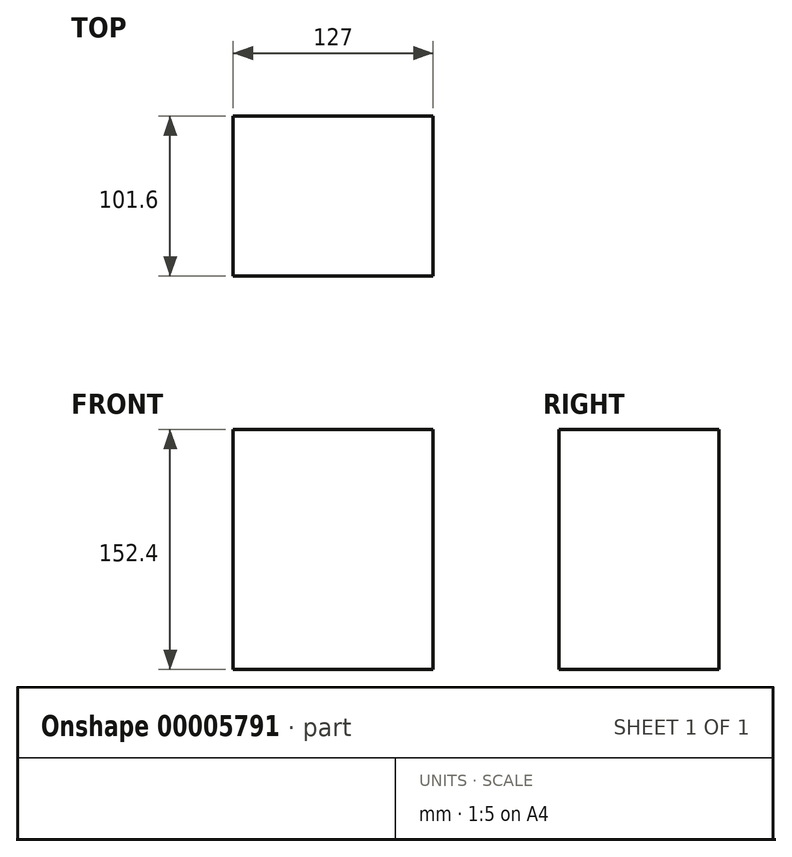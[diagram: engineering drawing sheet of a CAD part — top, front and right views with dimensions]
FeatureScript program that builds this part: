
annotation { "Feature Type Name" : "Feature", "Feature Type Description" : "" }
export const myFeature = defineFeature(function(context is Context, id is Id, definition is map)
    precondition{}
    {
        {
            var Q0;
            Q0=qCreatedBy(makeId("Top.planeOp"),FACE);
            var sketch = newSketch(context, id + "F0", { "sketchPlane" : qUnion([Q0])});
            skLineSegment(sketch, "E0.bottom", {"start": v(0, 0) * mm, "end": v(127, 0) * mm});
            skLineSegment(sketch, "E0.top", {"start": v(0, -101.6) * mm, "end": v(127, -101.6) * mm});
            skLineSegment(sketch, "E0.left", {"start": v(0, 0) * mm, "end": v(0, -101.6) * mm});
            skLineSegment(sketch, "E0.right", {"start": v(127, 0) * mm, "end": v(127, -101.6) * mm});
            skSolve(sketch);
        }
        {
            var Q0;
            Q0=makeQuery(id+"F0.imprint","IMPRINT",FACE,{"disambiguationData":[TD([[makeQuery(id+"F0.imprint","IMPRINT",EDGE,{"derivedFrom":sQuery(id+"F0.wireOp",EDGE,"E0.bottom")}),-1.0]])]});
            extrude(context, id + "F1", {"entities" : qUnion([Q0]), "depth" : 152.4 * mm});
        }
    });
